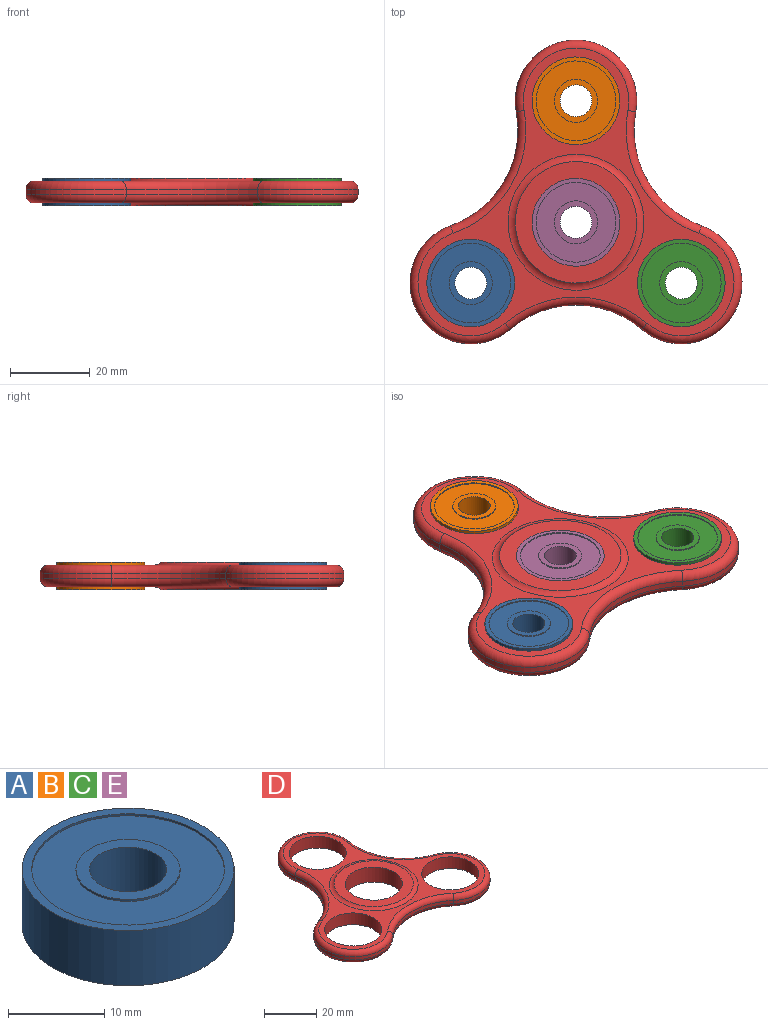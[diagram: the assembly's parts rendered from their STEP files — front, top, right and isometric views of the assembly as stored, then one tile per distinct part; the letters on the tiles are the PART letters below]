
ASSEMBLY  parts=5 mates=4
PART A: 12 faces, bbox 22x22x7 mm
  f0: plane 10.8x10.8mm, normal (0,0,-1), area 41.3mm2, adj f5,f11
  f1: plane 10.8x10.8mm, normal (0,0,1), area 41.3mm2, adj f5,f8
  f2: plane 22x22mm, normal (0,0,1), area 66.3mm2, adj f4,f6
  f3: plane 22x22mm, normal (0,0,-1), area 66.3mm2, adj f4,f10
  f4: cylinder r=11mm len=22mm, axis (0,0,-1), area 483.8mm2, adj f2,f3
  f5: cylinder r=4mm len=8mm, axis (0,0,-1), area 175.9mm2, adj f0,f1
  f6: cylinder r=9.99mm len=19.99mm, axis (0,0,1), area 16mm2, adj f2,f7
  f7: plane 19.99x19.99mm, normal (0,0,1), area 222.2mm2, adj f6,f8
  f8: cylinder r=5.4mm len=10.8mm, axis (0,0,1), area 8.6mm2, adj f1,f7
  f9: plane 19.99x19.99mm, normal (0,0,-1), area 222.2mm2, adj f10,f11
  f10: cylinder r=9.99mm len=19.99mm, axis (0,0,-1), area 16mm2, adj f3,f9
  f11: cylinder r=5.4mm len=10.8mm, axis (0,0,-1), area 8.6mm2, adj f0,f9
PART B: same geometry as A
PART C: same geometry as A
PART D: 28 faces, bbox 85.8x78.7x10.6 mm
  f0: cylinder r=11mm len=22mm, axis (0,0,-1), area 483.8mm2, adj f1,f2
  f1: plane 30.48x30.48mm, normal (0,0,1), area 349.5mm2, adj f0,f26
  f2: plane 30.48x30.48mm, normal (0,0,-1), area 349.5mm2, adj f0,f27
  f3: cylinder r=15.24mm len=30.48mm, axis (0,0,-1), area 80.2mm2, adj f4,f10,f17,f23
  f4: cylinder r=25.4mm len=28.58mm, axis (0,0,-1), area 53.9mm2, adj f3,f5,f19,f25
  f5: cylinder r=15.24mm len=29.61mm, axis (0,0,-1), area 80.2mm2, adj f4,f6,f18,f24
  f6: cylinder r=25.4mm len=33mm, axis (0,0,-1), area 53.9mm2, adj f5,f7,f16,f22
  f7: cylinder r=15.24mm len=29.61mm, axis (0,0,-1), area 80.2mm2, adj f6,f10,f14,f20
  f8: cylinder r=11mm len=22mm, axis (0,0,-1), area 380.1mm2, adj f12,f13
  f9: cylinder r=11mm len=22mm, axis (0,0,-1), area 380.1mm2, adj f12,f13
  f10: cylinder r=25.4mm len=28.58mm, axis (0,0,-1), area 53.9mm2, adj f3,f7,f15,f21
  f11: cylinder r=11mm len=22mm, axis (0,0,-1), area 380.1mm2, adj f12,f13
  f12: plane 79.27x72.2mm, normal (0,0,1), area 931.3mm2, adj f8,f9,f11,f20,f21,f22,f23,f24
  f13: plane 79.27x72.2mm, normal (0,0,-1), area 931.3mm2, adj f8,f9,f11,f14,f15,f16,f17,f18
  f14: torus R=13.24mm, axis (0,0,1), area 160mm2, adj f7,f13,f15,f16
  f15: torus R=27.4mm, axis (0,0,1), area 116.1mm2, adj f10,f13,f14,f17
  f16: torus R=27.4mm, axis (0,0,1), area 116.1mm2, adj f6,f13,f14,f18
  f17: torus R=13.24mm, axis (0,0,1), area 160mm2, adj f3,f13,f15,f19
  f18: torus R=13.24mm, axis (0,0,1), area 160mm2, adj f5,f13,f16,f19
  f19: torus R=27.4mm, axis (0,0,1), area 116.1mm2, adj f4,f13,f17,f18
  f20: torus R=13.24mm, axis (0,0,1), area 160mm2, adj f7,f12,f21,f22
  f21: torus R=27.4mm, axis (0,0,1), area 116.1mm2, adj f10,f12,f20,f23
  f22: torus R=27.4mm, axis (0,0,1), area 116.1mm2, adj f6,f12,f20,f24
  f23: torus R=13.24mm, axis (0,0,1), area 160mm2, adj f3,f12,f21,f25
  f24: torus R=13.24mm, axis (0,0,1), area 160mm2, adj f5,f12,f22,f25
  f25: torus R=27.4mm, axis (0,0,1), area 116.1mm2, adj f4,f12,f23,f24
  f26: torus R=17.04mm, axis (0,0,1), area 202.6mm2, adj f1,f12
  f27: torus R=17.04mm, axis (0,0,1), area 202.6mm2, adj f2,f13
PART E: same geometry as A
PLACE A t=(-25.3,-26.24,25.5)mm
PLACE B rot(axis=(0,0,1),0deg) t=(1.1,19.48,25.5)mm
PLACE C t=(27.5,-26.24,25.5)mm
PLACE D t=(1.1,-11,25.5)mm
PLACE E t=(1.1,-11,25.5)mm
MATE revolute D.f7 <-> C.f4  axis (0,0,-1) through (27.5,-26.24,25.5)mm
MATE revolute B.f4 <-> D.f11  axis (0,0,-1) through (1.1,19.48,25.5)mm
MATE revolute A.f4 <-> D.f5  axis (0,0,-1) through (-25.3,-26.24,25.5)mm
MATE revolute D.f0 <-> E.f4  axis (0,0,-1) through (1.1,-11,25.5)mm
